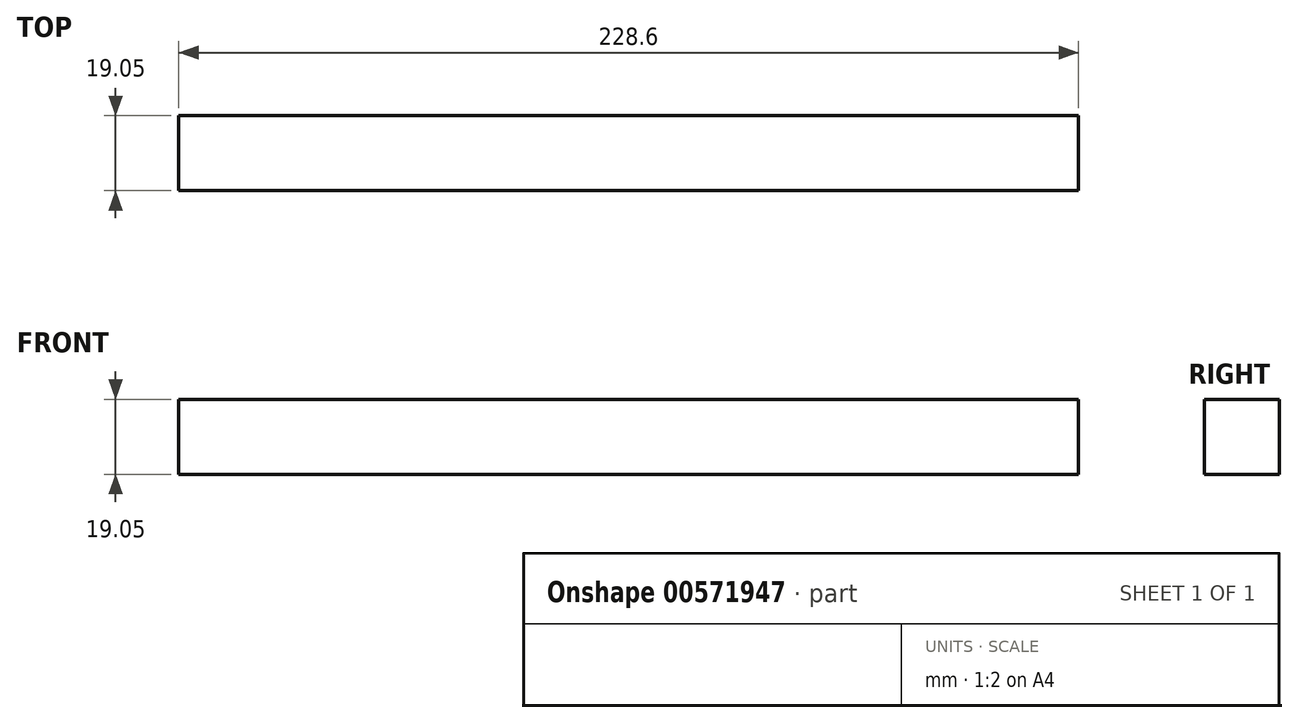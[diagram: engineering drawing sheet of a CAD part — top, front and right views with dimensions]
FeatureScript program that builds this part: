
annotation { "Feature Type Name" : "Feature", "Feature Type Description" : "" }
export const myFeature = defineFeature(function(context is Context, id is Id, definition is map)
    precondition{}
    {
        {
            var Q0;
            Q0=qCreatedBy(makeId("Top.planeOp"),FACE);
            var sketch = newSketch(context, id + "F0", { "sketchPlane" : qUnion([Q0])});
            skLineSegment(sketch, "E0.bottom", {"start": v(0, 0) * mm, "end": v(-228.6, 0) * mm});
            skLineSegment(sketch, "E0.top", {"start": v(0, 19.05) * mm, "end": v(-228.6, 19.05) * mm});
            skLineSegment(sketch, "E0.left", {"start": v(0, 0) * mm, "end": v(0, 19.05) * mm});
            skLineSegment(sketch, "E0.right", {"start": v(-228.6, 0) * mm, "end": v(-228.6, 19.05) * mm});
            skSolve(sketch);
        }
        {
            var Q0;
            Q0 = qSketchRegion(id + "F0", true);
            extrude(context, id + "F1", {"entities" : qUnion([Q0]), "depth" : 19.05 * mm, "offsetDistance" : 25.4 * mm});
        }
    });
